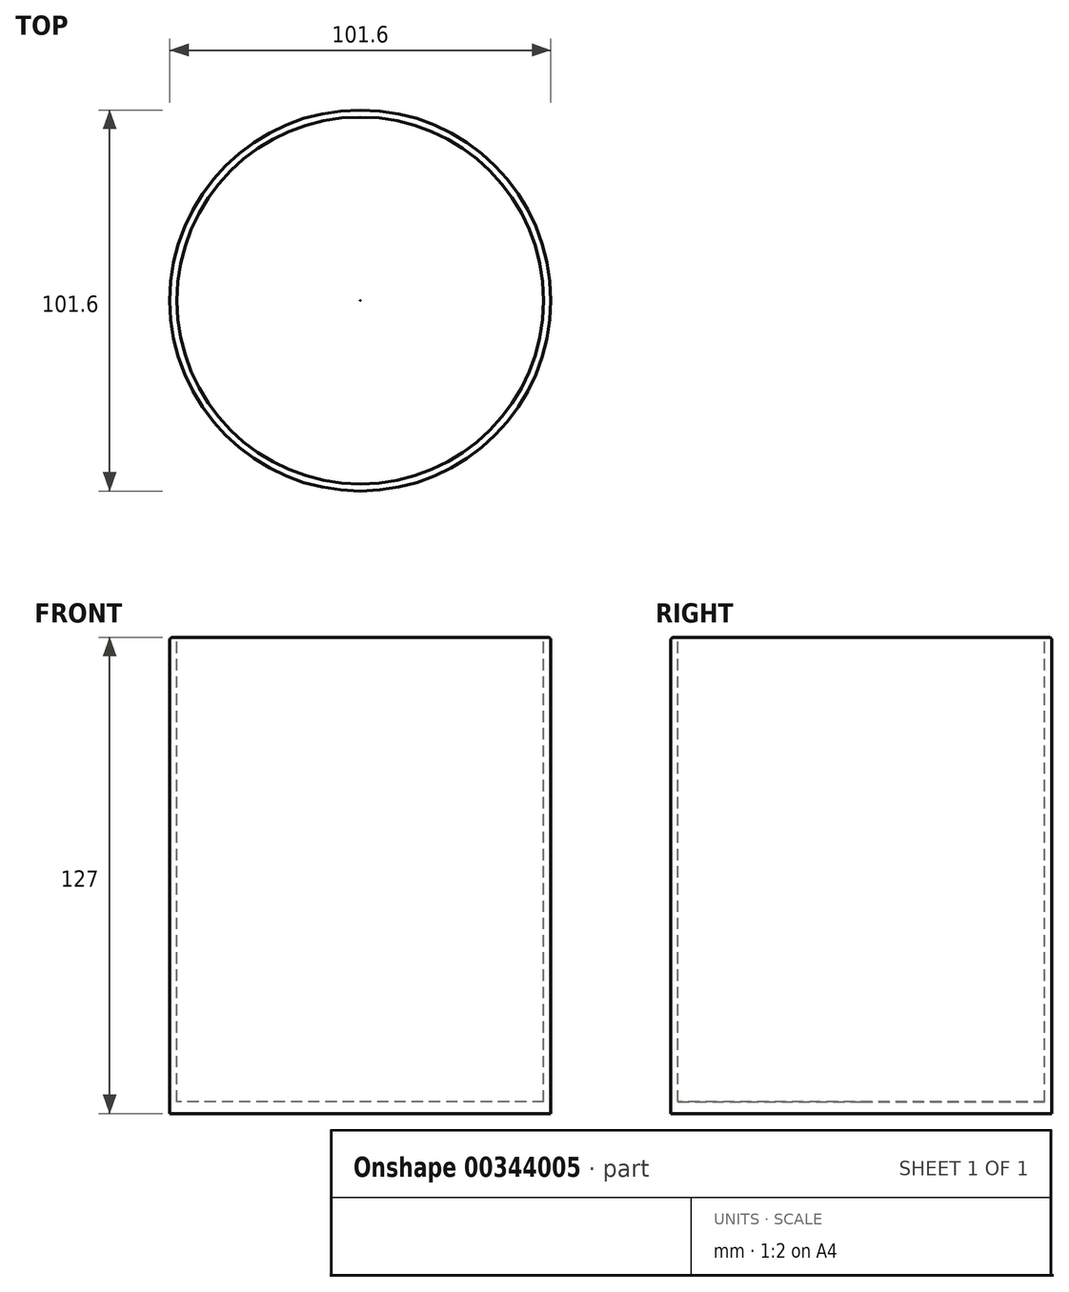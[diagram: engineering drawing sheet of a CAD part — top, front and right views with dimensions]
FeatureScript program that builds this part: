
annotation { "Feature Type Name" : "Feature", "Feature Type Description" : "" }
export const myFeature = defineFeature(function(context is Context, id is Id, definition is map)
    precondition{}
    {
        {
            var Q0;
            Q0=qCreatedBy(makeId("Top.planeOp"),FACE);
            var sketch = newSketch(context, id + "F0", { "sketchPlane" : qUnion([Q0])});
            skCircle(sketch, "E0", {"center": v(0, 0) * mm, "radius": 50.8 * mm});
            skSolve(sketch);
        }
        {
            var Q0;
            Q0 = qSketchRegion(id + "F0", true);
            extrude(context, id + "F1", {"entities" : qUnion([Q0]), "oppositeDirection" : true, "depth" : 127 * mm});
        }
        {
            var Q0;
            Q0=qCreatedBy(makeId("Top.planeOp"),FACE);
            var sketch = newSketch(context, id + "F2", { "sketchPlane" : qUnion([Q0])});
            skCircle(sketch, "E1", {"center": v(0, 0) * mm, "radius": 47.63 * mm});
            skSolve(sketch);
        }
        {
            var Q0;
            Q0=sQuery(id+"F2.wireOp",VERTEX,"E1.center");
            var Q1;
            Q1=makeQuery(id+"F1.opExtrude","SWEPT_BODY",BODY,{"disambiguationData":[OSD([sQuery(id+"F0.wireOp",EDGE,"E0")])]});
            hole(context, id + "F3", {"style" : HoleStyle.C_BORE, "endStyle" : HoleEndStyle.BLIND, "holeDiameter" : 0.03 * mm, "cBoreDiameter" : 97.8 * mm, "cBoreDepth" : 123.82 * mm, "holeDepth" : 123.82 * mm, "isTappedThrough" : true, "tappedDepth" : 12.7 * mm, "tapClearance" : 3, "startFromSketch" : true, "locations" : qUnion([Q0]), "scope" : qUnion([Q1])});
        }
        {
            var Q0;
            Q0=makeQuery(id+"F1.opExtrude","CAP_EDGE",EDGE,{"disambiguationData":[OSD([sQuery(id+"F0.wireOp",EDGE,"E0")])],"isStart":true});
            var Q1;
            Q1=makeQuery(id+"F3.hole-0.boolean.opBoolean","COPY",EDGE,{"derivedFrom":makeQuery(id+"F3.hole-0.opRevolve","SWEPT_EDGE",EDGE,{"disambiguationData":[OSD([sQuery(id+"F3.hole-0.sketch.wireOp",EDGE,"cbore_start_line_2"),sQuery(id+"F3.hole-0.sketch.wireOp",EDGE,"cbore_start_line_3")])]})});
            fillet(context, id + "F4", {"entities" : qUnion([Q0, Q1]), "radius" : 0.8 * mm, "tangentPropagation" : true, "allowEdgeOverflow" : false});
        }
    });
